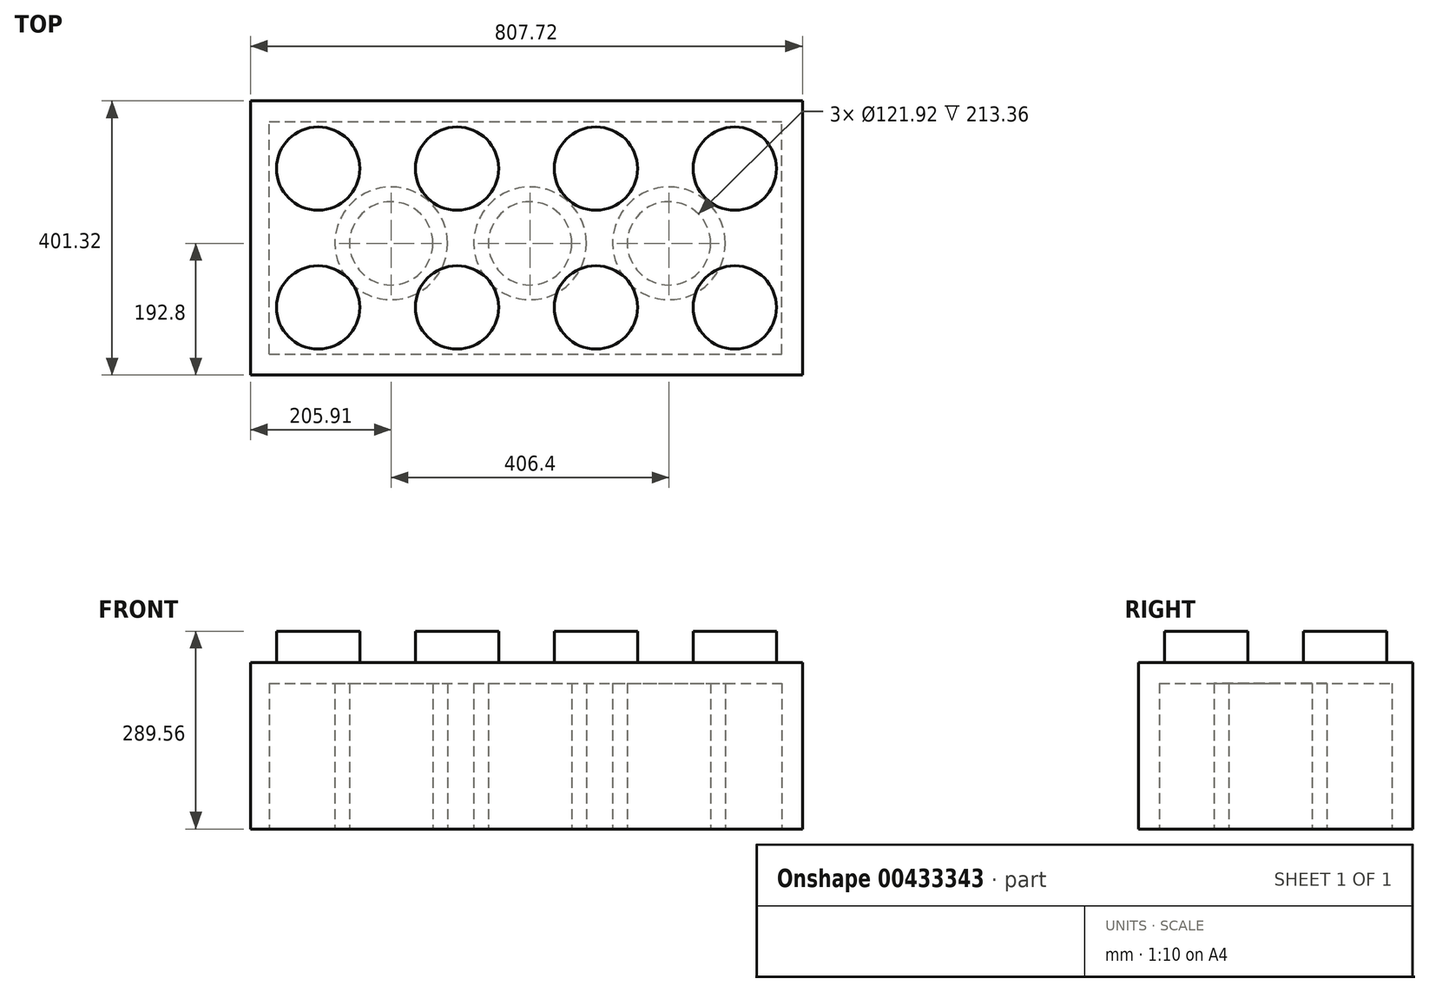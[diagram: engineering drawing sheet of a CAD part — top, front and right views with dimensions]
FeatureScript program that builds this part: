
annotation { "Feature Type Name" : "Feature", "Feature Type Description" : "" }
export const myFeature = defineFeature(function(context is Context, id is Id, definition is map)
    precondition{}
    {
        {
            var Q0;
            Q0=qCreatedBy(makeId("Top.planeOp"),FACE);
            var sketch = newSketch(context, id + "F0", { "sketchPlane" : qUnion([Q0])});
            skLineSegment(sketch, "E0.bottom", {"start": v(-409.11, 208.52) * mm, "end": v(398.6, 208.52) * mm});
            skLineSegment(sketch, "E0.top", {"start": v(-409.11, -192.8) * mm, "end": v(398.6, -192.8) * mm});
            skLineSegment(sketch, "E0.left", {"start": v(-409.11, 208.52) * mm, "end": v(-409.11, -192.8) * mm});
            skLineSegment(sketch, "E0.right", {"start": v(398.6, 208.52) * mm, "end": v(398.6, -192.8) * mm});
            skSolve(sketch);
        }
        {
            var Q0;
            Q0=makeQuery(id+"F0.imprint","IMPRINT",FACE,{"disambiguationData":[TD([[makeQuery(id+"F0.imprint","IMPRINT",EDGE,{"derivedFrom":sQuery(id+"F0.wireOp",EDGE,"E0.bottom")}),-1.0]])]});
            extrude(context, id + "F1", {"entities" : qUnion([Q0]), "depth" : 243.84 * mm});
        }
        {
            var Q0;
            Q0=makeQuery(id+"F1.opExtrude","CAP_FACE",FACE,{"disambiguationData":[OSD([sQuery(id+"F0.wireOp",EDGE,"E0.bottom"),sQuery(id+"F0.wireOp",EDGE,"E0.top"),sQuery(id+"F0.wireOp",EDGE,"E0.left"),sQuery(id+"F0.wireOp",EDGE,"E0.right")])],"isStart":false});
            var sketch = newSketch(context, id + "F2", { "sketchPlane" : qUnion([Q0])});
            skCircle(sketch, "E1", {"center": v(-310.05, 109.46) * mm, "radius": 60.96 * mm});
            skCircle(sketch, "E2.0.1.0", {"center": v(-310.05, -93.74) * mm, "radius": 60.96 * mm});
            skCircle(sketch, "E2.1.0.0", {"center": v(-106.85, 109.46) * mm, "radius": 60.96 * mm});
            skCircle(sketch, "E2.1.1.0", {"center": v(-106.85, -93.74) * mm, "radius": 60.96 * mm});
            skCircle(sketch, "E2.2.0.0", {"center": v(96.35, 109.46) * mm, "radius": 60.96 * mm});
            skCircle(sketch, "E2.2.1.0", {"center": v(96.35, -93.74) * mm, "radius": 60.96 * mm});
            skCircle(sketch, "E2.3.0.0", {"center": v(299.55, 109.46) * mm, "radius": 60.96 * mm});
            skCircle(sketch, "E2.3.1.0", {"center": v(299.55, -93.74) * mm, "radius": 60.96 * mm});
            skLineSegment(sketch, "E2.direction1", {"start": v(-310.05, 109.46) * mm, "end": v(-106.85, 109.46) * mm, "construction": true});
            skLineSegment(sketch, "E2.direction2", {"start": v(-310.05, 109.46) * mm, "end": v(-310.05, -93.74) * mm, "construction": true});
            skSolve(sketch);
        }
        {
            var Q0;
            Q0=qSketchRegion(id+"F2",true);
            extrude(context, id + "F3", {"entities" : qUnion([Q0]), "operationType" : NewBodyOperationType.ADD, "depth" : 45.72 * mm});
        }
        {
            var Q0;
            Q0=makeQuery(id+"F1.opExtrude","CAP_FACE",FACE,{"disambiguationData":[OSD([sQuery(id+"F0.wireOp",EDGE,"E0.bottom"),sQuery(id+"F0.wireOp",EDGE,"E0.top"),sQuery(id+"F0.wireOp",EDGE,"E0.left"),sQuery(id+"F0.wireOp",EDGE,"E0.right")])],"isStart":true});
            var sketch = newSketch(context, id + "F4", { "sketchPlane" : qUnion([Q0])});
            skLineSegment(sketch, "E3.bottom", {"start": v(-381.68, 162.32) * mm, "end": v(368.13, 162.32) * mm});
            skLineSegment(sketch, "E3.top", {"start": v(-381.68, -178.04) * mm, "end": v(368.13, -178.04) * mm});
            skLineSegment(sketch, "E3.left", {"start": v(-381.68, 162.32) * mm, "end": v(-381.68, -178.04) * mm});
            skLineSegment(sketch, "E3.right", {"start": v(368.13, 162.32) * mm, "end": v(368.13, -178.04) * mm});
            skCircle(sketch, "E4", {"center": v(0, 0) * mm, "radius": 82.55 * mm});
            skCircle(sketch, "E5", {"center": v(0, 0) * mm, "radius": 60.96 * mm});
            skCircle(sketch, "E6.1.0.0", {"center": v(-203.2, 0) * mm, "radius": 60.96 * mm});
            skCircle(sketch, "E6.1.0.1", {"center": v(-203.2, 0) * mm, "radius": 82.55 * mm});
            skLineSegment(sketch, "E6.direction1", {"start": v(0, 0) * mm, "end": v(-203.2, 0) * mm, "construction": true});
            skCircle(sketch, "E7.1.0.0", {"center": v(203.2, 0) * mm, "radius": 60.96 * mm});
            skCircle(sketch, "E7.1.0.1", {"center": v(203.2, 0) * mm, "radius": 82.55 * mm});
            skLineSegment(sketch, "E7.direction1", {"start": v(0, 0) * mm, "end": v(203.2, 0) * mm, "construction": true});
            skSolve(sketch);
        }
        {
            var Q0;
            Q0=makeQuery(id+"F4.imprint","IMPRINT",FACE,{"disambiguationData":[TD([[makeQuery(id+"F4.imprint","IMPRINT",EDGE,{"derivedFrom":sQuery(id+"F4.wireOp",EDGE,"E3.bottom")}),-1.0]])]});
            var Q1;
            Q1=makeQuery(id+"F4.imprint","IMPRINT",FACE,{"disambiguationData":[TD([[makeQuery(id+"F4.imprint","IMPRINT",EDGE,{"derivedFrom":sQuery(id+"F4.wireOp",EDGE,"E6.1.0.0")}),1.0]])]});
            var Q2;
            Q2=makeQuery(id+"F4.imprint","IMPRINT",FACE,{"disambiguationData":[TD([[makeQuery(id+"F4.imprint","IMPRINT",EDGE,{"derivedFrom":sQuery(id+"F4.wireOp",EDGE,"E5")}),1.0]])]});
            var Q3;
            Q3=makeQuery(id+"F4.imprint","IMPRINT",FACE,{"disambiguationData":[TD([[makeQuery(id+"F4.imprint","IMPRINT",EDGE,{"derivedFrom":sQuery(id+"F4.wireOp",EDGE,"E7.1.0.0")}),1.0]])]});
            extrude(context, id + "F5", {"entities" : qUnion([Q0, Q1, Q2, Q3]), "operationType" : NewBodyOperationType.REMOVE, "oppositeDirection" : true, "depth" : 213.36 * mm});
        }
    });
